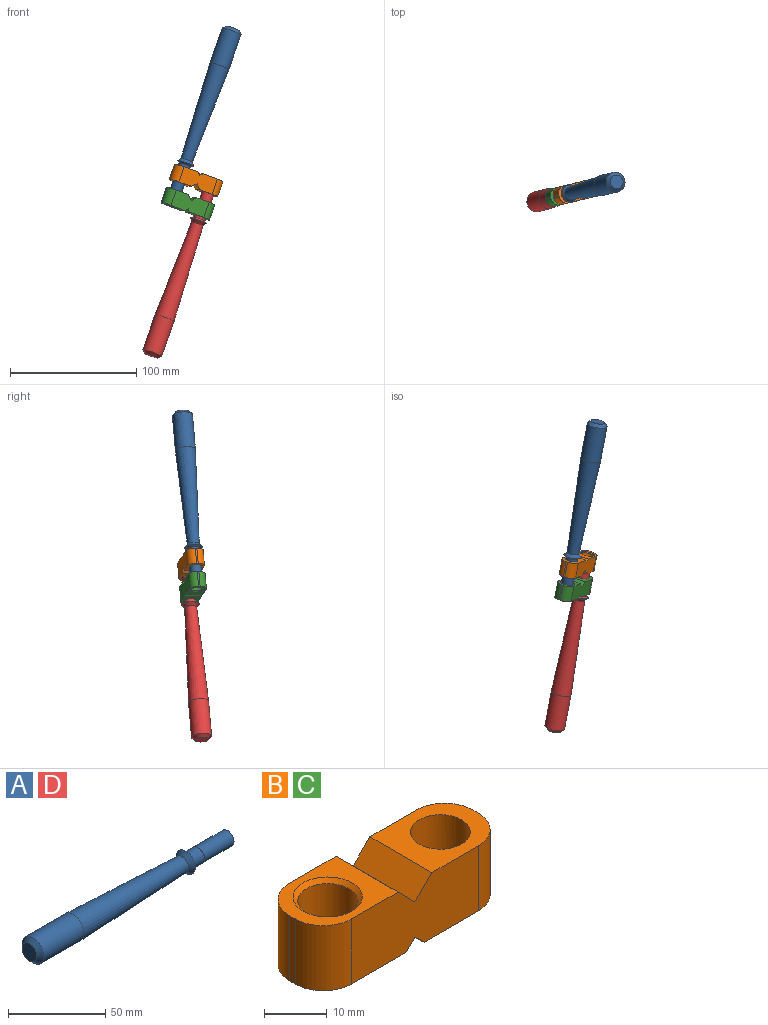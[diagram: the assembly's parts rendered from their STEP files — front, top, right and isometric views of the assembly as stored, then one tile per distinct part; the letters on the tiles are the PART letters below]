
ASSEMBLY  parts=4 mates=3
PART A: 11 faces, bbox 144.1x15.9x15.9 mm
  f0: cylinder r=7.95mm len=29.21mm, axis (-1,0,0), area 1459.1mm2, adj f1,f8
  f1: cone r=7.95mm half-angle=2.3deg, axis (-1,0,0), area 3175.8mm2, adj f0,f2
  f2: cone r=4.78mm half-angle=41deg, axis (1,0,0), area 124.4mm2, adj f1,f3
  f3: plane 13.97x13.97mm, normal (1,0,0), area 38.5mm2, adj f2,f9
  f4: cylinder r=4.78mm len=9.55mm, axis (-1,0,0), area 228.6mm2, adj f9,f10
  f5: cylinder r=4.7mm len=21.51mm, axis (-1,0,0), area 635.2mm2, adj f6,f10
  f6: plane 9.4x9.4mm, normal (1,0,0), area 69.4mm2, adj f5
  f7: plane 10.82x10.82mm, normal (-1,0,0), area 92mm2, adj f8
  f8: cone r=5.41mm half-angle=45deg, axis (1,0,0), area 150.8mm2, adj f0,f7
  f9: cone r=6.05mm half-angle=45deg, axis (-1,0,0), area 61.1mm2, adj f3,f4
  f10: cone r=4.78mm half-angle=45deg, axis (-1,0,0), area 3.2mm2, adj f4,f5
PART B: 20 faces, bbox 41.3x14x12.7 mm
  f0: plane 12.7x1.27mm, normal (1,0,0), area 16.1mm2, adj f1,f9,f17,f19
  f1: plane 16.83x13.97mm, normal (0,0,1), area 146.5mm2, adj f0,f2,f10,f11,f12,f17,f19
  f2: plane 13.97x3.81mm, normal (-0.71,0,0.71), area 75.3mm2, adj f1,f3,f10,f11
  f3: plane 13.97x3.81mm, normal (0.71,0,0.71), area 75.3mm2, adj f2,f4,f10,f11
  f4: plane 16.83x13.97mm, normal (0,0,1), area 121.9mm2, adj f3,f5,f10,f11,f14,f16,f18
  f5: plane 12.7x1.27mm, normal (-1,0,0), area 16.1mm2, adj f4,f6,f16,f18
  f6: plane 18.61x13.97mm, normal (0,0,-1), area 146.7mm2, adj f5,f7,f10,f11,f15,f16,f18
  f7: plane 13.97x2.03mm, normal (0.71,0,-0.71), area 40.1mm2, adj f6,f8,f10,f11
  f8: plane 13.97x2.03mm, normal (-0.71,0,-0.71), area 40.1mm2, adj f7,f9,f10,f11
  f9: plane 18.61x13.97mm, normal (0,0,-1), area 171.4mm2, adj f0,f8,f10,f11,f12,f17,f19
  f10: plane 28.58x12.7mm, normal (0,-1,0), area 344.3mm2, adj f1,f2,f3,f4,f6,f7,f8,f9
  f11: plane 28.58x12.7mm, normal (0,1,0), area 344.3mm2, adj f1,f2,f3,f4,f6,f7,f8,f9
  f12: cylinder r=4.76mm len=12.7mm, axis (0,0,1), area 380mm2, adj f1,f9
  f13: cylinder r=4.76mm len=11.18mm, axis (0,0,1), area 334.4mm2, adj f14,f15
  f14: cone r=4.76mm half-angle=45deg, axis (0,0,1), area 34.8mm2, adj f4,f13
  f15: cone r=4.76mm half-angle=45deg, axis (0,0,-1), area 34.8mm2, adj f6,f13
  f16: cylinder r=6.35mm len=12.7mm, axis (0,0,-1), area 126.7mm2, adj f4,f5,f6,f11
  f17: cylinder r=6.35mm len=12.7mm, axis (0,0,1), area 126.7mm2, adj f0,f1,f9,f11
  f18: cylinder r=6.35mm len=12.7mm, axis (0,0,1), area 126.7mm2, adj f4,f5,f6,f10
  f19: cylinder r=6.35mm len=12.7mm, axis (0,0,-1), area 126.7mm2, adj f0,f1,f9,f10
PART C: same geometry as B
PART D: same geometry as A
PLACE A rot(axis=(-0.12,0.99,0.08),110.3deg) t=(37.42,-58.74,-22.07)mm
PLACE B rot(axis=(0.12,-0.99,0.02),160.4deg) t=(6.78,-58.93,-142.67)mm
PLACE C rot(axis=(-0.1,0.82,0.56),23.9deg) t=(0.34,-60.48,-161.11)mm
PLACE D rot(axis=(0.73,-0.39,0.56),116.5deg) t=(-26.99,-74.25,-281.57)mm
MATE slider B.f13 <-> D.f0  axis (0.33,0.08,0.94) through (18.2,-63.37,-152.22)mm
MATE slider A.f0 <-> C.f13  axis (0.33,0.08,0.94) through (-1.62,-68.14,-133.82)mm
MATE slider D.f0 <-> C.f12  axis (-0.33,-0.08,-0.94) through (13.3,-64.55,-166.23)mm
